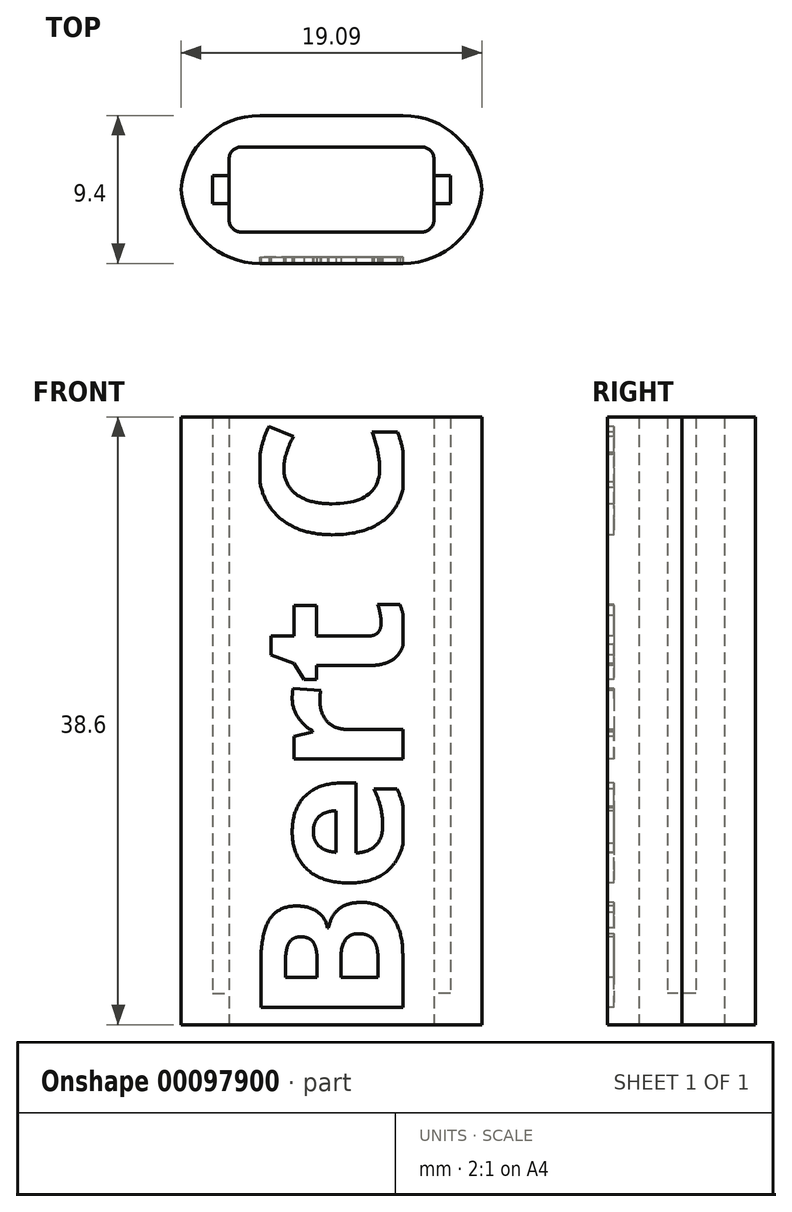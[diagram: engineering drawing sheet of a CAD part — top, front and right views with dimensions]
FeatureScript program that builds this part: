
annotation { "Feature Type Name" : "Feature", "Feature Type Description" : "" }
export const myFeature = defineFeature(function(context is Context, id is Id, definition is map)
    precondition{}
    {
        {
            var Q0;
            Q0=qCreatedBy(makeId("Top.planeOp"),FACE);
            var sketch = newSketch(context, id + "F0", { "sketchPlane" : qUnion([Q0])});
            skLineSegment(sketch, "E0.bottom", {"start": v(-21.71, 12.23) * mm, "end": v(-10.21, 12.23) * mm});
            skLineSegment(sketch, "E0.top", {"start": v(-21.71, 7.83) * mm, "end": v(-10.21, 7.83) * mm});
            skLineSegment(sketch, "E0.left", {"start": v(-21.96, 11.98) * mm, "end": v(-21.96, 10.43) * mm});
            skLineSegment(sketch, "E0.right", {"start": v(-9.96, 11.98) * mm, "end": v(-9.96, 10.43) * mm});
            skPoint(sketch, "E1.visualSharp", {"position": v(-21.96, 12.23) * mm});
            skArc(sketch, "E1.filletArc", {"start": v(-21.71, 12.23) * mm, "mid": v(-21.9, 12.15) * mm, "end": v(-21.96, 11.98) * mm});
            skPoint(sketch, "E2.visualSharp", {"position": v(-21.96, 7.83) * mm});
            skArc(sketch, "E2.filletArc", {"start": v(-21.96, 8.08) * mm, "mid": v(-21.9, 7.9) * mm, "end": v(-21.71, 7.83) * mm});
            skPoint(sketch, "E3.visualSharp", {"position": v(-9.96, 12.23) * mm});
            skArc(sketch, "E3.filletArc", {"start": v(-9.96, 11.98) * mm, "mid": v(-10.04, 12.15) * mm, "end": v(-10.21, 12.23) * mm});
            skPoint(sketch, "E4.visualSharp", {"position": v(-9.96, 7.83) * mm});
            skArc(sketch, "E4.filletArc", {"start": v(-10.21, 7.83) * mm, "mid": v(-10.04, 7.9) * mm, "end": v(-9.96, 8.08) * mm});
            skPoint(sketch, "E5", {"position": v(-21.96, 10.03) * mm});
            skPoint(sketch, "E6", {"position": v(-9.96, 10.03) * mm});
            skLineSegment(sketch, "E7", {"start": v(-21.96, 10.03) * mm, "end": v(-23.01, 10.03) * mm});
            skLineSegment(sketch, "E8", {"start": v(-9.96, 10.03) * mm, "end": v(-8.91, 10.03) * mm});
            skLineSegment(sketch, "E9", {"start": v(-23.01, 10.03) * mm, "end": v(-23.01, 10.43) * mm});
            skLineSegment(sketch, "E10", {"start": v(-23.01, 10.43) * mm, "end": v(-21.96, 10.43) * mm});
            skLineSegment(sketch, "E11", {"start": v(-23.01, 10.03) * mm, "end": v(-23.01, 9.63) * mm});
            skLineSegment(sketch, "E12", {"start": v(-23.01, 9.63) * mm, "end": v(-21.96, 9.63) * mm});
            skLineSegment(sketch, "E13", {"start": v(-8.91, 10.03) * mm, "end": v(-8.91, 9.63) * mm});
            skLineSegment(sketch, "E14", {"start": v(-8.91, 9.63) * mm, "end": v(-9.96, 9.63) * mm});
            skLineSegment(sketch, "E15", {"start": v(-8.91, 10.03) * mm, "end": v(-8.91, 10.43) * mm});
            skLineSegment(sketch, "E16", {"start": v(-8.91, 10.43) * mm, "end": v(-9.96, 10.43) * mm});
            skPoint(sketch, "E17.end.orphan", {"position": v(-23.01, 12.23) * mm});
            skPoint(sketch, "E18.orphan", {"position": v(-23.01, 7.83) * mm});
            skPoint(sketch, "E19.end.orphan", {"position": v(-8.91, 12.23) * mm});
            skPoint(sketch, "E20.orphan", {"position": v(-8.91, 7.83) * mm});
            skLineSegment(sketch, "E21", {"start": v(-21.96, 10.43) * mm, "end": v(-21.96, 9.63) * mm});
            skLineSegment(sketch, "E22", {"start": v(-21.96, 9.63) * mm, "end": v(-21.96, 8.08) * mm});
            skLineSegment(sketch, "E23", {"start": v(-9.96, 9.63) * mm, "end": v(-9.96, 8.08) * mm});
            skLineSegment(sketch, "E24", {"start": v(-9.96, 10.43) * mm, "end": v(-9.96, 9.63) * mm});
            skLineSegment(sketch, "E25.0", {"start": v(-8.41, 9.13) * mm, "end": v(-9.46, 9.13) * mm});
            skLineSegment(sketch, "E25.1", {"start": v(-8.41, 10.03) * mm, "end": v(-8.41, 9.13) * mm});
            skLineSegment(sketch, "E25.2", {"start": v(-8.41, 10.03) * mm, "end": v(-8.41, 10.93) * mm});
            skLineSegment(sketch, "E25.3", {"start": v(-8.41, 10.93) * mm, "end": v(-9.46, 10.93) * mm});
            skLineSegment(sketch, "E25.4", {"start": v(-9.46, 11.98) * mm, "end": v(-9.46, 10.93) * mm});
            skLineSegment(sketch, "E25.5", {"start": v(-9.46, 9.13) * mm, "end": v(-9.46, 8.08) * mm});
            skArc(sketch, "E25.6", {"start": v(-9.46, 11.98) * mm, "mid": v(-9.68, 12.5) * mm, "end": v(-10.21, 12.73) * mm});
            skLineSegment(sketch, "E25.7", {"start": v(-21.71, 12.73) * mm, "end": v(-10.21, 12.73) * mm});
            skLineSegment(sketch, "E25.8", {"start": v(-22.46, 9.13) * mm, "end": v(-22.46, 8.08) * mm});
            skArc(sketch, "E25.9", {"start": v(-22.46, 8.08) * mm, "mid": v(-22.24, 7.55) * mm, "end": v(-21.71, 7.33) * mm});
            skLineSegment(sketch, "E25.10", {"start": v(-21.71, 7.33) * mm, "end": v(-10.21, 7.33) * mm});
            skArc(sketch, "E25.11", {"start": v(-10.21, 7.33) * mm, "mid": v(-9.68, 7.55) * mm, "end": v(-9.46, 8.08) * mm});
            skLineSegment(sketch, "E25.12", {"start": v(-23.51, 9.13) * mm, "end": v(-22.46, 9.13) * mm});
            skLineSegment(sketch, "E25.13", {"start": v(-23.51, 10.03) * mm, "end": v(-23.51, 9.13) * mm});
            skLineSegment(sketch, "E25.14", {"start": v(-23.51, 10.03) * mm, "end": v(-23.51, 10.93) * mm});
            skLineSegment(sketch, "E25.15", {"start": v(-23.51, 10.93) * mm, "end": v(-22.46, 10.93) * mm});
            skLineSegment(sketch, "E25.16", {"start": v(-22.46, 11.98) * mm, "end": v(-22.46, 10.93) * mm});
            skArc(sketch, "E25.17", {"start": v(-21.71, 12.73) * mm, "mid": v(-22.24, 12.5) * mm, "end": v(-22.46, 11.98) * mm});
            skLineSegment(sketch, "E26.0", {"start": v(-20.51, 14.73) * mm, "end": v(-11.41, 14.73) * mm});
            skLineSegment(sketch, "E27.0", {"start": v(-25.51, 10.33) * mm, "end": v(-25.51, 10.03) * mm});
            skLineSegment(sketch, "E28.0", {"start": v(-20.51, 5.33) * mm, "end": v(-11.41, 5.33) * mm});
            skLineSegment(sketch, "E29.0", {"start": v(-6.41, 9.73) * mm, "end": v(-6.41, 10.03) * mm});
            skLineSegment(sketch, "E29.1", {"start": v(-6.41, 10.33) * mm, "end": v(-6.41, 10.03) * mm});
            skLineSegment(sketch, "E30", {"start": v(-25.51, 9.73) * mm, "end": v(-25.51, 10.03) * mm});
            skPoint(sketch, "E31.orphan", {"position": v(-21.71, 14.73) * mm});
            skPoint(sketch, "E32.visualSharp", {"position": v(-25.51, 14.73) * mm});
            skArc(sketch, "E32.filletArc", {"start": v(-20.51, 14.73) * mm, "mid": v(-24.05, 13.26) * mm, "end": v(-25.51, 9.73) * mm});
            skPoint(sketch, "E33.visualSharp", {"position": v(-6.41, 14.73) * mm});
            skArc(sketch, "E33.filletArc", {"start": v(-6.41, 9.73) * mm, "mid": v(-7.88, 13.26) * mm, "end": v(-11.41, 14.73) * mm});
            skPoint(sketch, "E34.visualSharp", {"position": v(-6.41, 5.33) * mm});
            skArc(sketch, "E34.filletArc", {"start": v(-11.41, 5.33) * mm, "mid": v(-7.88, 6.8) * mm, "end": v(-6.41, 10.33) * mm});
            skPoint(sketch, "E35.visualSharp", {"position": v(-25.51, 5.33) * mm});
            skArc(sketch, "E35.filletArc", {"start": v(-25.51, 10.33) * mm, "mid": v(-24.05, 6.8) * mm, "end": v(-20.51, 5.33) * mm});
            skLineSegment(sketch, "E36", {"start": v(-22.46, 10.93) * mm, "end": v(-22.46, 9.13) * mm});
            skLineSegment(sketch, "E37", {"start": v(-9.46, 10.93) * mm, "end": v(-9.46, 9.13) * mm});
            skSolve(sketch);
        }
        {
            var Q0;
            Q0=makeQuery(id+"F0.imprint","IMPRINT",FACE,{"disambiguationData":[TD([[makeQuery(id+"F0.imprint","IMPRINT",EDGE,{"derivedFrom":sQuery(id+"F0.wireOp",EDGE,"E25.0")}),1.0]])]});
            extrude(context, id + "F1", {"entities" : qUnion([Q0]), "depth" : 36.6 * mm});
        }
        {
            var Q0;
            Q0=makeQuery(id+"F0.imprint","IMPRINT",FACE,{"disambiguationData":[TD([[makeQuery(id+"F0.imprint","IMPRINT",EDGE,{"derivedFrom":sQuery(id+"F0.wireOp",EDGE,"E25.0")}),1.0]])]});
            var Q1;
            {var subQ4=sQuery(id+"F0.wireOp",EDGE,"E9");Q1=makeQuery(id+"F0.imprint","IMPRINT",FACE,{"disambiguationData":[TD([[makeQuery(id+"F0.imprint","IMPRINT",EDGE,{"derivedFrom":subQ4}),1.0]])]});}
            var Q2;
            {var subQ6=sQuery(id+"F0.wireOp",EDGE,"E13");Q2=makeQuery(id+"F0.imprint","IMPRINT",FACE,{"disambiguationData":[TD([[makeQuery(id+"F0.imprint","IMPRINT",EDGE,{"derivedFrom":subQ6}),1.0]])]});}
            var Q3;
            {var subQ0=sQuery(id+"F0.wireOp",EDGE,"E15");Q3=makeQuery(id+"F0.imprint","IMPRINT",FACE,{"disambiguationData":[TD([[makeQuery(id+"F0.imprint","IMPRINT",EDGE,{"derivedFrom":subQ0}),1.0]])]});}
            var Q4;
            {var subQ0=sQuery(id+"F0.wireOp",EDGE,"E13");Q4=makeQuery(id+"F0.imprint","IMPRINT",FACE,{"disambiguationData":[TD([[makeQuery(id+"F0.imprint","IMPRINT",EDGE,{"derivedFrom":subQ0}),-1.0]])]});}
            var Q5;
            {var subQ0=sQuery(id+"F0.wireOp",EDGE,"E11");Q5=makeQuery(id+"F0.imprint","IMPRINT",FACE,{"disambiguationData":[TD([[makeQuery(id+"F0.imprint","IMPRINT",EDGE,{"derivedFrom":subQ0}),1.0]])]});}
            var Q6;
            {var subQ0=sQuery(id+"F0.wireOp",EDGE,"E9");Q6=makeQuery(id+"F0.imprint","IMPRINT",FACE,{"disambiguationData":[TD([[makeQuery(id+"F0.imprint","IMPRINT",EDGE,{"derivedFrom":subQ0}),-1.0]])]});}
            extrude(context, id + "F2", {"entities" : qUnion([Q0, Q1, Q2, Q3, Q4, Q5, Q6]), "operationType" : NewBodyOperationType.ADD, "oppositeDirection" : true, "depth" : 2 * mm});
        }
        {
            var Q0;
            {var subQ0=sQuery(id+"F0.wireOp",EDGE,"E28.0");Q0=makeQuery(id+"F2.boolean.opBoolean","MERGE",FACE,{"derivedFrom":[makeQuery(id+"F1.opExtrude","SWEPT_FACE",FACE,{"disambiguationData":[OSD([subQ0])]}),makeQuery(id+"F2.opExtrude","SWEPT_FACE",FACE,{"disambiguationData":[OSD([subQ0])]})]});}
            var sketch = newSketch(context, id + "F3", { "sketchPlane" : qUnion([Q0])});
            skText(sketch, "E38", { "text": "Bert C", "fontName": "OpenSans-Bold.ttf"});
            skLineSegment(sketch, "E39.0", {"start": v(-20.51, 36.6) * mm, "end": v(-11.41, 36.6) * mm});
            skLineSegment(sketch, "E39.1", {"start": v(-20.51, 36.6) * mm, "end": v(-20.51, -2) * mm});
            skLineSegment(sketch, "E39.2", {"start": v(-20.51, -2) * mm, "end": v(-11.41, -2) * mm});
            skLineSegment(sketch, "E39.3", {"start": v(-11.41, 36.6) * mm, "end": v(-11.41, -2) * mm});
            const initialGuessF3  = {"E38": [-0.01144, -0.00205, 0, 1, 0.00909]};
            skSetInitialGuess(sketch, initialGuessF3);
            skSolve(sketch);
        }
        {
            var Q0;
            Q0=makeQuery(id+"F3.imprint","IMPRINT",FACE,{"disambiguationData":[TD([[makeQuery(id+"F3.imprint","IMPRINT",EDGE,{"derivedFrom":sQuery(id+"F3.wireOp",EDGE,"E38.sketch_text.stroke-76")}),-1.0]])]});
            var Q1;
            Q1=makeQuery(id+"F3.imprint","IMPRINT",FACE,{"disambiguationData":[TD([[makeQuery(id+"F3.imprint","IMPRINT",EDGE,{"derivedFrom":sQuery(id+"F3.wireOp",EDGE,"E38.sketch_text.stroke-58")}),-1.0]])]});
            var Q2;
            Q2=makeQuery(id+"F3.imprint","IMPRINT",FACE,{"disambiguationData":[TD([[makeQuery(id+"F3.imprint","IMPRINT",EDGE,{"derivedFrom":sQuery(id+"F3.wireOp",EDGE,"E38.sketch_text.stroke-45")}),-1.0]])]});
            var Q3;
            Q3=makeQuery(id+"F3.imprint","IMPRINT",FACE,{"disambiguationData":[TD([[makeQuery(id+"F3.imprint","IMPRINT",EDGE,{"derivedFrom":sQuery(id+"F3.wireOp",EDGE,"E38.sketch_text.stroke-25")}),-1.0]])]});
            var Q4;
            Q4=makeQuery(id+"F3.imprint","IMPRINT",FACE,{"disambiguationData":[TD([[makeQuery(id+"F3.imprint","IMPRINT",EDGE,{"derivedFrom":sQuery(id+"F3.wireOp",EDGE,"E38.sketch_text.stroke-0")}),-1.0]])]});
            extrude(context, id + "F4", {"entities" : qUnion([Q0, Q1, Q2, Q3, Q4]), "operationType" : NewBodyOperationType.REMOVE, "oppositeDirection" : true, "depth" : .4 * mm});
        }
    });
